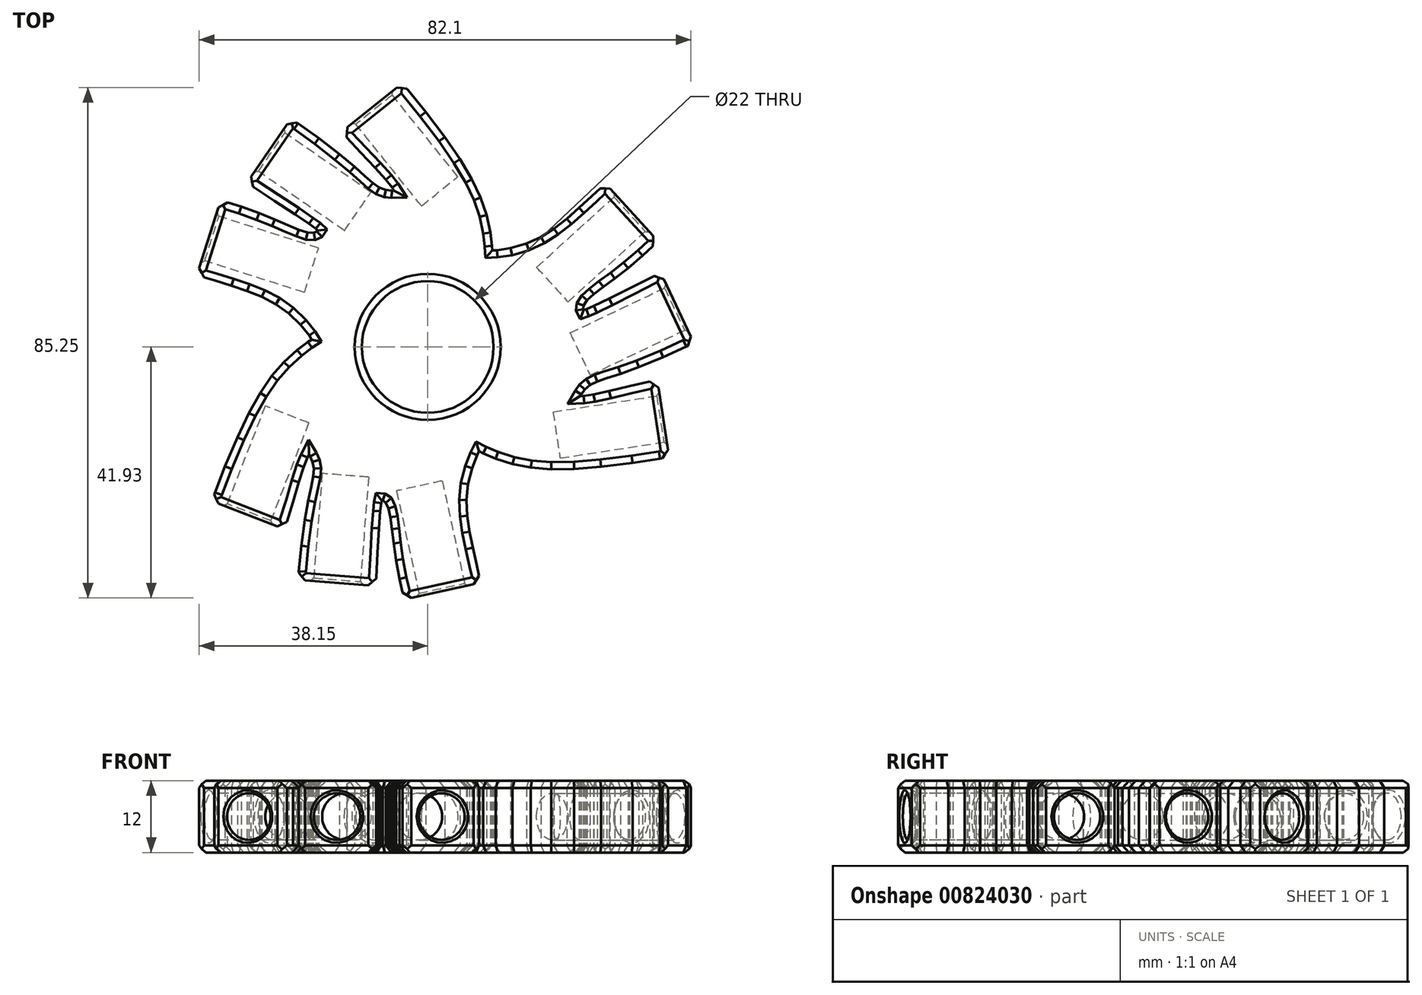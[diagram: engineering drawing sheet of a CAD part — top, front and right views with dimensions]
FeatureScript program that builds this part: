
annotation { "Feature Type Name" : "Feature", "Feature Type Description" : "" }
export const myFeature = defineFeature(function(context is Context, id is Id, definition is map)
    precondition{}
    {
        {
            var Q0;
            Q0=qCreatedBy(makeId("Top.planeOp"),FACE);
            var sketch = newSketch(context, id + "F0", { "sketchPlane" : qUnion([Q0])});
            skLineSegment(sketch, "E0", {"start": v(-3.87, -42.17) * mm, "end": v(8.83, -39.4) * mm});
            skLineSegment(sketch, "E1", {"start": v(8.83, -39.4) * mm, "end": v(8.67, -38.64) * mm});
            skLineSegment(sketch, "E2", {"start": v(8.67, -38.64) * mm, "end": v(8.17, -36.4) * mm});
            skLineSegment(sketch, "E3", {"start": v(8.17, -36.4) * mm, "end": v(7.52, -33.55) * mm});
            skLineSegment(sketch, "E4", {"start": v(7.52, -33.55) * mm, "end": v(6.96, -30.83) * mm});
            skLineSegment(sketch, "E5", {"start": v(6.96, -30.83) * mm, "end": v(6.6, -28.19) * mm});
            skLineSegment(sketch, "E6", {"start": v(6.6, -28.19) * mm, "end": v(6.48, -25.57) * mm});
            skLineSegment(sketch, "E7", {"start": v(6.48, -25.57) * mm, "end": v(6.72, -22.93) * mm});
            skLineSegment(sketch, "E8", {"start": v(6.72, -22.93) * mm, "end": v(7.4, -20.23) * mm});
            skLineSegment(sketch, "E9", {"start": v(7.4, -20.23) * mm, "end": v(8.24, -18.1) * mm});
            skLineSegment(sketch, "E10", {"start": v(8.24, -18.1) * mm, "end": v(8.6, -17.42) * mm});
            skLineSegment(sketch, "E11", {"start": v(8.6, -17.42) * mm, "end": v(9.26, -17.76) * mm});
            skLineSegment(sketch, "E12", {"start": v(9.26, -17.76) * mm, "end": v(11.34, -18.65) * mm});
            skLineSegment(sketch, "E13", {"start": v(11.34, -18.65) * mm, "end": v(14.16, -19.56) * mm});
            skLineSegment(sketch, "E14", {"start": v(14.16, -19.56) * mm, "end": v(17.2, -20.15) * mm});
            skLineSegment(sketch, "E15", {"start": v(17.2, -20.15) * mm, "end": v(20.6, -20.42) * mm});
            skLineSegment(sketch, "E16", {"start": v(20.6, -20.42) * mm, "end": v(24.46, -20.37) * mm});
            skLineSegment(sketch, "E17", {"start": v(24.46, -20.37) * mm, "end": v(28.95, -20.02) * mm});
            skLineSegment(sketch, "E18", {"start": v(28.95, -20.02) * mm, "end": v(34.19, -19.35) * mm});
            skLineSegment(sketch, "E19", {"start": v(34.19, -19.35) * mm, "end": v(38.78, -18.65) * mm});
            skLineSegment(sketch, "E20", {"start": v(38.78, -18.65) * mm, "end": v(40.3, -18.39) * mm});
            skLineSegment(sketch, "E21", {"start": v(40.3, -18.39) * mm, "end": v(38.33, -5.54) * mm});
            skLineSegment(sketch, "E22", {"start": v(38.33, -5.54) * mm, "end": v(37.16, -5.78) * mm});
            skLineSegment(sketch, "E23", {"start": v(37.16, -5.78) * mm, "end": v(33.7, -6.57) * mm});
            skLineSegment(sketch, "E24", {"start": v(33.7, -6.57) * mm, "end": v(30.3, -7.38) * mm});
            skLineSegment(sketch, "E25", {"start": v(30.3, -7.38) * mm, "end": v(27.7, -7.94) * mm});
            skLineSegment(sketch, "E26", {"start": v(27.7, -7.94) * mm, "end": v(26.02, -8.19) * mm});
            skLineSegment(sketch, "E27", {"start": v(26.02, -8.19) * mm, "end": v(25.45, -8.22) * mm});
            skLineSegment(sketch, "E28", {"start": v(25.45, -8.22) * mm, "end": v(25.62, -7.92) * mm});
            skLineSegment(sketch, "E29", {"start": v(25.62, -7.92) * mm, "end": v(26.22, -7.09) * mm});
            skLineSegment(sketch, "E30", {"start": v(26.22, -7.09) * mm, "end": v(27.1, -6.34) * mm});
            skLineSegment(sketch, "E31", {"start": v(27.1, -6.34) * mm, "end": v(28.29, -5.78) * mm});
            skLineSegment(sketch, "E32", {"start": v(28.29, -5.78) * mm, "end": v(29.92, -5.22) * mm});
            skLineSegment(sketch, "E33", {"start": v(29.92, -5.22) * mm, "end": v(32.2, -4.48) * mm});
            skLineSegment(sketch, "E34", {"start": v(32.2, -4.48) * mm, "end": v(35.26, -3.38) * mm});
            skLineSegment(sketch, "E35", {"start": v(35.26, -3.38) * mm, "end": v(39.3, -1.73) * mm});
            skLineSegment(sketch, "E36", {"start": v(39.3, -1.73) * mm, "end": v(43.18, 0.04) * mm});
            skLineSegment(sketch, "E37", {"start": v(43.18, 0.04) * mm, "end": v(44.46, 0.66) * mm});
            skLineSegment(sketch, "E38", {"start": v(44.46, 0.66) * mm, "end": v(38.88, 12.4) * mm});
            skLineSegment(sketch, "E39", {"start": v(38.88, 12.4) * mm, "end": v(37.64, 11.78) * mm});
            skLineSegment(sketch, "E40", {"start": v(37.64, 11.78) * mm, "end": v(33.94, 9.92) * mm});
            skLineSegment(sketch, "E41", {"start": v(33.94, 9.92) * mm, "end": v(30.3, 8.08) * mm});
            skLineSegment(sketch, "E42", {"start": v(30.3, 8.08) * mm, "end": v(27.73, 6.83) * mm});
            skLineSegment(sketch, "E43", {"start": v(27.73, 6.83) * mm, "end": v(26.49, 6.28) * mm});
            skLineSegment(sketch, "E44", {"start": v(26.49, 6.28) * mm, "end": v(26.06, 6.14) * mm});
            skLineSegment(sketch, "E45", {"start": v(26.06, 6.14) * mm, "end": v(25.98, 6.3) * mm});
            skLineSegment(sketch, "E46", {"start": v(25.98, 6.3) * mm, "end": v(26.03, 6.93) * mm});
            skLineSegment(sketch, "E47", {"start": v(26.03, 6.93) * mm, "end": v(26.62, 7.8) * mm});
            skLineSegment(sketch, "E48", {"start": v(26.62, 7.8) * mm, "end": v(27.73, 8.8) * mm});
            skLineSegment(sketch, "E49", {"start": v(27.73, 8.8) * mm, "end": v(29.3, 10) * mm});
            skLineSegment(sketch, "E50", {"start": v(29.3, 10) * mm, "end": v(31.24, 11.44) * mm});
            skLineSegment(sketch, "E51", {"start": v(31.24, 11.44) * mm, "end": v(33.46, 13.17) * mm});
            skLineSegment(sketch, "E52", {"start": v(33.46, 13.17) * mm, "end": v(35.89, 15.24) * mm});
            skLineSegment(sketch, "E53", {"start": v(35.89, 15.24) * mm, "end": v(37.83, 17.06) * mm});
            skLineSegment(sketch, "E54", {"start": v(37.83, 17.06) * mm, "end": v(38.44, 17.7) * mm});
            skLineSegment(sketch, "E55", {"start": v(38.44, 17.7) * mm, "end": v(29.69, 27.3) * mm});
            skLineSegment(sketch, "E56", {"start": v(29.69, 27.3) * mm, "end": v(29.11, 26.8) * mm});
            skLineSegment(sketch, "E57", {"start": v(29.11, 26.8) * mm, "end": v(27.42, 25.23) * mm});
            skLineSegment(sketch, "E58", {"start": v(27.42, 25.23) * mm, "end": v(25.28, 23.25) * mm});
            skLineSegment(sketch, "E59", {"start": v(25.28, 23.25) * mm, "end": v(23.2, 21.41) * mm});
            skLineSegment(sketch, "E60", {"start": v(23.2, 21.41) * mm, "end": v(21.1, 19.77) * mm});
            skLineSegment(sketch, "E61", {"start": v(21.1, 19.77) * mm, "end": v(18.89, 18.37) * mm});
            skLineSegment(sketch, "E62", {"start": v(18.89, 18.37) * mm, "end": v(16.48, 17.26) * mm});
            skLineSegment(sketch, "E63", {"start": v(16.48, 17.26) * mm, "end": v(13.8, 16.5) * mm});
            skLineSegment(sketch, "E64", {"start": v(13.8, 16.5) * mm, "end": v(11.53, 16.15) * mm});
            skLineSegment(sketch, "E65", {"start": v(11.53, 16.15) * mm, "end": v(10.77, 16.12) * mm});
            skLineSegment(sketch, "E66", {"start": v(10.77, 16.12) * mm, "end": v(10.73, 16.87) * mm});
            skLineSegment(sketch, "E67", {"start": v(10.73, 16.87) * mm, "end": v(10.47, 19.11) * mm});
            skLineSegment(sketch, "E68", {"start": v(10.47, 19.11) * mm, "end": v(9.84, 22.01) * mm});
            skLineSegment(sketch, "E69", {"start": v(9.84, 22.01) * mm, "end": v(8.83, 24.94) * mm});
            skLineSegment(sketch, "E70", {"start": v(8.83, 24.94) * mm, "end": v(7.37, 28) * mm});
            skLineSegment(sketch, "E71", {"start": v(7.37, 28) * mm, "end": v(5.4, 31.34) * mm});
            skLineSegment(sketch, "E72", {"start": v(5.4, 31.34) * mm, "end": v(2.84, 35.05) * mm});
            skLineSegment(sketch, "E73", {"start": v(2.84, 35.05) * mm, "end": v(-0.35, 39.25) * mm});
            skLineSegment(sketch, "E74", {"start": v(-0.35, 39.25) * mm, "end": v(-3.26, 42.87) * mm});
            skLineSegment(sketch, "E75", {"start": v(-3.26, 42.87) * mm, "end": v(-4.24, 44.06) * mm});
            skLineSegment(sketch, "E76", {"start": v(-4.24, 44.06) * mm, "end": v(-14.38, 35.92) * mm});
            skLineSegment(sketch, "E77", {"start": v(-14.38, 35.92) * mm, "end": v(-13.6, 35.04) * mm});
            skLineSegment(sketch, "E78", {"start": v(-13.6, 35.04) * mm, "end": v(-11.17, 32.43) * mm});
            skLineSegment(sketch, "E79", {"start": v(-11.17, 32.43) * mm, "end": v(-8.77, 29.9) * mm});
            skLineSegment(sketch, "E80", {"start": v(-8.77, 29.9) * mm, "end": v(-7, 27.93) * mm});
            skLineSegment(sketch, "E81", {"start": v(-7, 27.93) * mm, "end": v(-5.94, 26.59) * mm});
            skLineSegment(sketch, "E82", {"start": v(-5.94, 26.59) * mm, "end": v(-5.63, 26.11) * mm});
            skLineSegment(sketch, "E83", {"start": v(-5.63, 26.11) * mm, "end": v(-5.97, 26.1) * mm});
            skLineSegment(sketch, "E84", {"start": v(-5.97, 26.1) * mm, "end": v(-6.99, 26.21) * mm});
            skLineSegment(sketch, "E85", {"start": v(-6.99, 26.21) * mm, "end": v(-8.08, 26.6) * mm});
            skLineSegment(sketch, "E86", {"start": v(-8.08, 26.6) * mm, "end": v(-9.16, 27.35) * mm});
            skLineSegment(sketch, "E87", {"start": v(-9.16, 27.35) * mm, "end": v(-10.46, 28.5) * mm});
            skLineSegment(sketch, "E88", {"start": v(-10.46, 28.5) * mm, "end": v(-12.23, 30.09) * mm});
            skLineSegment(sketch, "E89", {"start": v(-12.23, 30.09) * mm, "end": v(-14.72, 32.2) * mm});
            skLineSegment(sketch, "E90", {"start": v(-14.72, 32.2) * mm, "end": v(-18.17, 34.86) * mm});
            skLineSegment(sketch, "E91", {"start": v(-18.17, 34.86) * mm, "end": v(-21.64, 37.35) * mm});
            skLineSegment(sketch, "E92", {"start": v(-21.64, 37.35) * mm, "end": v(-22.82, 38.14) * mm});
            skLineSegment(sketch, "E93", {"start": v(-22.82, 38.14) * mm, "end": v(-30.2, 27.43) * mm});
            skLineSegment(sketch, "E94", {"start": v(-30.2, 27.43) * mm, "end": v(-29.04, 26.67) * mm});
            skLineSegment(sketch, "E95", {"start": v(-29.04, 26.67) * mm, "end": v(-25.58, 24.4) * mm});
            skLineSegment(sketch, "E96", {"start": v(-25.58, 24.4) * mm, "end": v(-22.16, 22.16) * mm});
            skLineSegment(sketch, "E97", {"start": v(-22.16, 22.16) * mm, "end": v(-19.8, 20.56) * mm});
            skLineSegment(sketch, "E98", {"start": v(-19.8, 20.56) * mm, "end": v(-18.7, 19.76) * mm});
            skLineSegment(sketch, "E99", {"start": v(-18.7, 19.76) * mm, "end": v(-18.36, 19.46) * mm});
            skLineSegment(sketch, "E100", {"start": v(-18.36, 19.46) * mm, "end": v(-18.46, 19.31) * mm});
            skLineSegment(sketch, "E101", {"start": v(-18.46, 19.31) * mm, "end": v(-19.03, 19.04) * mm});
            skLineSegment(sketch, "E102", {"start": v(-19.03, 19.04) * mm, "end": v(-20.08, 19.11) * mm});
            skLineSegment(sketch, "E103", {"start": v(-20.08, 19.11) * mm, "end": v(-21.51, 19.58) * mm});
            skLineSegment(sketch, "E104", {"start": v(-21.51, 19.58) * mm, "end": v(-23.33, 20.34) * mm});
            skLineSegment(sketch, "E105", {"start": v(-23.33, 20.34) * mm, "end": v(-25.54, 21.3) * mm});
            skLineSegment(sketch, "E106", {"start": v(-25.54, 21.3) * mm, "end": v(-28.15, 22.36) * mm});
            skLineSegment(sketch, "E107", {"start": v(-28.15, 22.36) * mm, "end": v(-31.16, 23.43) * mm});
            skLineSegment(sketch, "E108", {"start": v(-31.16, 23.43) * mm, "end": v(-33.7, 24.2) * mm});
            skLineSegment(sketch, "E109", {"start": v(-33.7, 24.2) * mm, "end": v(-34.56, 24.4) * mm});
            skLineSegment(sketch, "E110", {"start": v(-34.56, 24.4) * mm, "end": v(-38.5, 12.02) * mm});
            skLineSegment(sketch, "E111", {"start": v(-38.5, 12.02) * mm, "end": v(-37.78, 11.78) * mm});
            skLineSegment(sketch, "E112", {"start": v(-37.78, 11.78) * mm, "end": v(-35.58, 11.1) * mm});
            skLineSegment(sketch, "E113", {"start": v(-35.58, 11.1) * mm, "end": v(-32.8, 10.23) * mm});
            skLineSegment(sketch, "E114", {"start": v(-32.8, 10.23) * mm, "end": v(-30.16, 9.35) * mm});
            skLineSegment(sketch, "E115", {"start": v(-30.16, 9.35) * mm, "end": v(-27.69, 8.35) * mm});
            skLineSegment(sketch, "E116", {"start": v(-27.69, 8.35) * mm, "end": v(-25.36, 7.14) * mm});
            skLineSegment(sketch, "E117", {"start": v(-25.36, 7.14) * mm, "end": v(-23.2, 5.61) * mm});
            skLineSegment(sketch, "E118", {"start": v(-23.2, 5.61) * mm, "end": v(-21.2, 3.68) * mm});
            skLineSegment(sketch, "E119", {"start": v(-21.2, 3.68) * mm, "end": v(-19.77, 1.88) * mm});
            skLineSegment(sketch, "E120", {"start": v(-19.77, 1.88) * mm, "end": v(-19.36, 1.24) * mm});
            skLineSegment(sketch, "E121", {"start": v(-19.36, 1.24) * mm, "end": v(-20, 0.83) * mm});
            skLineSegment(sketch, "E122", {"start": v(-20, 0.83) * mm, "end": v(-21.8, -0.52) * mm});
            skLineSegment(sketch, "E123", {"start": v(-21.8, -0.52) * mm, "end": v(-24, -2.52) * mm});
            skLineSegment(sketch, "E124", {"start": v(-24, -2.52) * mm, "end": v(-26.03, -4.86) * mm});
            skLineSegment(sketch, "E125", {"start": v(-26.03, -4.86) * mm, "end": v(-27.96, -7.66) * mm});
            skLineSegment(sketch, "E126", {"start": v(-27.96, -7.66) * mm, "end": v(-29.85, -11.03) * mm});
            skLineSegment(sketch, "E127", {"start": v(-29.85, -11.03) * mm, "end": v(-31.79, -15.1) * mm});
            skLineSegment(sketch, "E128", {"start": v(-31.79, -15.1) * mm, "end": v(-33.83, -19.96) * mm});
            skLineSegment(sketch, "E129", {"start": v(-33.83, -19.96) * mm, "end": v(-35.51, -24.3) * mm});
            skLineSegment(sketch, "E130", {"start": v(-35.51, -24.3) * mm, "end": v(-36.05, -25.74) * mm});
            skLineSegment(sketch, "E131", {"start": v(-36.05, -25.74) * mm, "end": v(-23.94, -30.45) * mm});
            skLineSegment(sketch, "E132", {"start": v(-23.94, -30.45) * mm, "end": v(-23.57, -29.33) * mm});
            skLineSegment(sketch, "E133", {"start": v(-23.57, -29.33) * mm, "end": v(-22.52, -25.92) * mm});
            skLineSegment(sketch, "E134", {"start": v(-22.52, -25.92) * mm, "end": v(-21.52, -22.58) * mm});
            skLineSegment(sketch, "E135", {"start": v(-21.52, -22.58) * mm, "end": v(-20.7, -20.06) * mm});
            skLineSegment(sketch, "E136", {"start": v(-20.7, -20.06) * mm, "end": v(-20.07, -18.47) * mm});
            skLineSegment(sketch, "E137", {"start": v(-20.07, -18.47) * mm, "end": v(-19.82, -17.97) * mm});
            skLineSegment(sketch, "E138", {"start": v(-19.82, -17.97) * mm, "end": v(-19.64, -18.26) * mm});
            skLineSegment(sketch, "E139", {"start": v(-19.64, -18.26) * mm, "end": v(-19.23, -19.2) * mm});
            skLineSegment(sketch, "E140", {"start": v(-19.23, -19.2) * mm, "end": v(-19.02, -20.34) * mm});
            skLineSegment(sketch, "E141", {"start": v(-19.02, -20.34) * mm, "end": v(-19.12, -21.64) * mm});
            skLineSegment(sketch, "E142", {"start": v(-19.12, -21.64) * mm, "end": v(-19.46, -23.34) * mm});
            skLineSegment(sketch, "E143", {"start": v(-19.46, -23.34) * mm, "end": v(-19.96, -25.67) * mm});
            skLineSegment(sketch, "E144", {"start": v(-19.96, -25.67) * mm, "end": v(-20.53, -28.88) * mm});
            skLineSegment(sketch, "E145", {"start": v(-20.53, -28.88) * mm, "end": v(-21.12, -33.2) * mm});
            skLineSegment(sketch, "E146", {"start": v(-21.12, -33.2) * mm, "end": v(-21.54, -37.45) * mm});
            skLineSegment(sketch, "E147", {"start": v(-21.54, -37.45) * mm, "end": v(-21.64, -38.87) * mm});
            skLineSegment(sketch, "E148", {"start": v(-21.64, -38.87) * mm, "end": v(-8.68, -39.9) * mm});
            skLineSegment(sketch, "E149", {"start": v(-8.68, -39.9) * mm, "end": v(-8.6, -38.52) * mm});
            skLineSegment(sketch, "E150", {"start": v(-8.6, -38.52) * mm, "end": v(-8.36, -34.39) * mm});
            skLineSegment(sketch, "E151", {"start": v(-8.36, -34.39) * mm, "end": v(-8.13, -30.3) * mm});
            skLineSegment(sketch, "E152", {"start": v(-8.13, -30.3) * mm, "end": v(-7.92, -27.46) * mm});
            skLineSegment(sketch, "E153", {"start": v(-7.92, -27.46) * mm, "end": v(-7.78, -26.11) * mm});
            skLineSegment(sketch, "E154", {"start": v(-7.78, -26.11) * mm, "end": v(-7.69, -25.67) * mm});
            skLineSegment(sketch, "E155", {"start": v(-7.69, -25.67) * mm, "end": v(-7.51, -25.68) * mm});
            skLineSegment(sketch, "E156", {"start": v(-7.51, -25.68) * mm, "end": v(-7, -26.04) * mm});
            skLineSegment(sketch, "E157", {"start": v(-7, -26.04) * mm, "end": v(-6.53, -26.98) * mm});
            skLineSegment(sketch, "E158", {"start": v(-6.53, -26.98) * mm, "end": v(-6.22, -28.45) * mm});
            skLineSegment(sketch, "E159", {"start": v(-6.22, -28.45) * mm, "end": v(-5.96, -30.41) * mm});
            skLineSegment(sketch, "E160", {"start": v(-5.96, -30.41) * mm, "end": v(-5.69, -32.8) * mm});
            skLineSegment(sketch, "E161", {"start": v(-5.69, -32.8) * mm, "end": v(-5.3, -35.6) * mm});
            skLineSegment(sketch, "E162", {"start": v(-5.3, -35.6) * mm, "end": v(-4.73, -38.73) * mm});
            skLineSegment(sketch, "E163", {"start": v(-4.73, -38.73) * mm, "end": v(-4.12, -41.32) * mm});
            skLineSegment(sketch, "E164", {"start": v(-4.12, -41.32) * mm, "end": v(-3.87, -42.17) * mm});
            skCircle(sketch, "E165", {"center": v(0, 0) * mm, "radius": 11 * mm});
            skSolve(sketch);
        }
        {
            var Q0;
            Q0=makeQuery(id+"F0.imprint","IMPRINT",FACE,{"disambiguationData":[TD([[makeQuery(id+"F0.imprint","IMPRINT",EDGE,{"derivedFrom":sQuery(id+"F0.wireOp",EDGE,"E0")}),1.0]])]});
            extrude(context, id + "F1", {"entities" : qUnion([Q0]), "endBound" : BoundingType.SYMMETRIC, "depth" : 12 * mm, "offsetDistance" : 25 * mm});
        }
        {
            var Q0;
            Q0=makeQuery(id+"F1.opExtrude","CAP_FACE",FACE,{"disambiguationData":[OSD([sQuery(id+"F0.wireOp",EDGE,"E0"),sQuery(id+"F0.wireOp",EDGE,"E1"),sQuery(id+"F0.wireOp",EDGE,"E2"),sQuery(id+"F0.wireOp",EDGE,"E3"),sQuery(id+"F0.wireOp",EDGE,"E4"),sQuery(id+"F0.wireOp",EDGE,"E5"),sQuery(id+"F0.wireOp",EDGE,"E6"),sQuery(id+"F0.wireOp",EDGE,"E7"),sQuery(id+"F0.wireOp",EDGE,"E8"),sQuery(id+"F0.wireOp",EDGE,"E9"),sQuery(id+"F0.wireOp",EDGE,"E10"),sQuery(id+"F0.wireOp",EDGE,"E11"),sQuery(id+"F0.wireOp",EDGE,"E12"),sQuery(id+"F0.wireOp",EDGE,"E13"),sQuery(id+"F0.wireOp",EDGE,"E14"),sQuery(id+"F0.wireOp",EDGE,"E15"),sQuery(id+"F0.wireOp",EDGE,"E16"),sQuery(id+"F0.wireOp",EDGE,"E17"),sQuery(id+"F0.wireOp",EDGE,"E18"),sQuery(id+"F0.wireOp",EDGE,"E19"),sQuery(id+"F0.wireOp",EDGE,"E20"),sQuery(id+"F0.wireOp",EDGE,"E21"),sQuery(id+"F0.wireOp",EDGE,"E22"),sQuery(id+"F0.wireOp",EDGE,"E23"),sQuery(id+"F0.wireOp",EDGE,"E24"),sQuery(id+"F0.wireOp",EDGE,"E25"),sQuery(id+"F0.wireOp",EDGE,"E26"),sQuery(id+"F0.wireOp",EDGE,"E27"),sQuery(id+"F0.wireOp",EDGE,"E28"),sQuery(id+"F0.wireOp",EDGE,"E29"),sQuery(id+"F0.wireOp",EDGE,"E30"),sQuery(id+"F0.wireOp",EDGE,"E31"),sQuery(id+"F0.wireOp",EDGE,"E32"),sQuery(id+"F0.wireOp",EDGE,"E33"),sQuery(id+"F0.wireOp",EDGE,"E34"),sQuery(id+"F0.wireOp",EDGE,"E35"),sQuery(id+"F0.wireOp",EDGE,"E36"),sQuery(id+"F0.wireOp",EDGE,"E37"),sQuery(id+"F0.wireOp",EDGE,"E38"),sQuery(id+"F0.wireOp",EDGE,"E39"),sQuery(id+"F0.wireOp",EDGE,"E40"),sQuery(id+"F0.wireOp",EDGE,"E41"),sQuery(id+"F0.wireOp",EDGE,"E42"),sQuery(id+"F0.wireOp",EDGE,"E43"),sQuery(id+"F0.wireOp",EDGE,"E44"),sQuery(id+"F0.wireOp",EDGE,"E45"),sQuery(id+"F0.wireOp",EDGE,"E46"),sQuery(id+"F0.wireOp",EDGE,"E47"),sQuery(id+"F0.wireOp",EDGE,"E48"),sQuery(id+"F0.wireOp",EDGE,"E49"),sQuery(id+"F0.wireOp",EDGE,"E50"),sQuery(id+"F0.wireOp",EDGE,"E51"),sQuery(id+"F0.wireOp",EDGE,"E52"),sQuery(id+"F0.wireOp",EDGE,"E53"),sQuery(id+"F0.wireOp",EDGE,"E54"),sQuery(id+"F0.wireOp",EDGE,"E55"),sQuery(id+"F0.wireOp",EDGE,"E56"),sQuery(id+"F0.wireOp",EDGE,"E57"),sQuery(id+"F0.wireOp",EDGE,"E58"),sQuery(id+"F0.wireOp",EDGE,"E59"),sQuery(id+"F0.wireOp",EDGE,"E60"),sQuery(id+"F0.wireOp",EDGE,"E61"),sQuery(id+"F0.wireOp",EDGE,"E62"),sQuery(id+"F0.wireOp",EDGE,"E63"),sQuery(id+"F0.wireOp",EDGE,"E64"),sQuery(id+"F0.wireOp",EDGE,"E65"),sQuery(id+"F0.wireOp",EDGE,"E66"),sQuery(id+"F0.wireOp",EDGE,"E67"),sQuery(id+"F0.wireOp",EDGE,"E68"),sQuery(id+"F0.wireOp",EDGE,"E69"),sQuery(id+"F0.wireOp",EDGE,"E70"),sQuery(id+"F0.wireOp",EDGE,"E71"),sQuery(id+"F0.wireOp",EDGE,"E72"),sQuery(id+"F0.wireOp",EDGE,"E73"),sQuery(id+"F0.wireOp",EDGE,"E74"),sQuery(id+"F0.wireOp",EDGE,"E75"),sQuery(id+"F0.wireOp",EDGE,"E76"),sQuery(id+"F0.wireOp",EDGE,"E77"),sQuery(id+"F0.wireOp",EDGE,"E78"),sQuery(id+"F0.wireOp",EDGE,"E79"),sQuery(id+"F0.wireOp",EDGE,"E80"),sQuery(id+"F0.wireOp",EDGE,"E81"),sQuery(id+"F0.wireOp",EDGE,"E82"),sQuery(id+"F0.wireOp",EDGE,"E83"),sQuery(id+"F0.wireOp",EDGE,"E84"),sQuery(id+"F0.wireOp",EDGE,"E85"),sQuery(id+"F0.wireOp",EDGE,"E86"),sQuery(id+"F0.wireOp",EDGE,"E87"),sQuery(id+"F0.wireOp",EDGE,"E88"),sQuery(id+"F0.wireOp",EDGE,"E89"),sQuery(id+"F0.wireOp",EDGE,"E90"),sQuery(id+"F0.wireOp",EDGE,"E91"),sQuery(id+"F0.wireOp",EDGE,"E92"),sQuery(id+"F0.wireOp",EDGE,"E93"),sQuery(id+"F0.wireOp",EDGE,"E94"),sQuery(id+"F0.wireOp",EDGE,"E95"),sQuery(id+"F0.wireOp",EDGE,"E96"),sQuery(id+"F0.wireOp",EDGE,"E97"),sQuery(id+"F0.wireOp",EDGE,"E98"),sQuery(id+"F0.wireOp",EDGE,"E99"),sQuery(id+"F0.wireOp",EDGE,"E100"),sQuery(id+"F0.wireOp",EDGE,"E101"),sQuery(id+"F0.wireOp",EDGE,"E102"),sQuery(id+"F0.wireOp",EDGE,"E103"),sQuery(id+"F0.wireOp",EDGE,"E104"),sQuery(id+"F0.wireOp",EDGE,"E105"),sQuery(id+"F0.wireOp",EDGE,"E106"),sQuery(id+"F0.wireOp",EDGE,"E107"),sQuery(id+"F0.wireOp",EDGE,"E108"),sQuery(id+"F0.wireOp",EDGE,"E109"),sQuery(id+"F0.wireOp",EDGE,"E110"),sQuery(id+"F0.wireOp",EDGE,"E111"),sQuery(id+"F0.wireOp",EDGE,"E112"),sQuery(id+"F0.wireOp",EDGE,"E113"),sQuery(id+"F0.wireOp",EDGE,"E114"),sQuery(id+"F0.wireOp",EDGE,"E115"),sQuery(id+"F0.wireOp",EDGE,"E116"),sQuery(id+"F0.wireOp",EDGE,"E117"),sQuery(id+"F0.wireOp",EDGE,"E118"),sQuery(id+"F0.wireOp",EDGE,"E119"),sQuery(id+"F0.wireOp",EDGE,"E120"),sQuery(id+"F0.wireOp",EDGE,"E121"),sQuery(id+"F0.wireOp",EDGE,"E122"),sQuery(id+"F0.wireOp",EDGE,"E123"),sQuery(id+"F0.wireOp",EDGE,"E124"),sQuery(id+"F0.wireOp",EDGE,"E125"),sQuery(id+"F0.wireOp",EDGE,"E126"),sQuery(id+"F0.wireOp",EDGE,"E127"),sQuery(id+"F0.wireOp",EDGE,"E128"),sQuery(id+"F0.wireOp",EDGE,"E129"),sQuery(id+"F0.wireOp",EDGE,"E130"),sQuery(id+"F0.wireOp",EDGE,"E131"),sQuery(id+"F0.wireOp",EDGE,"E132"),sQuery(id+"F0.wireOp",EDGE,"E133"),sQuery(id+"F0.wireOp",EDGE,"E134"),sQuery(id+"F0.wireOp",EDGE,"E135"),sQuery(id+"F0.wireOp",EDGE,"E136"),sQuery(id+"F0.wireOp",EDGE,"E137"),sQuery(id+"F0.wireOp",EDGE,"E138"),sQuery(id+"F0.wireOp",EDGE,"E139"),sQuery(id+"F0.wireOp",EDGE,"E140"),sQuery(id+"F0.wireOp",EDGE,"E141"),sQuery(id+"F0.wireOp",EDGE,"E142"),sQuery(id+"F0.wireOp",EDGE,"E143"),sQuery(id+"F0.wireOp",EDGE,"E144"),sQuery(id+"F0.wireOp",EDGE,"E145"),sQuery(id+"F0.wireOp",EDGE,"E146"),sQuery(id+"F0.wireOp",EDGE,"E147"),sQuery(id+"F0.wireOp",EDGE,"E148"),sQuery(id+"F0.wireOp",EDGE,"E149"),sQuery(id+"F0.wireOp",EDGE,"E150"),sQuery(id+"F0.wireOp",EDGE,"E151"),sQuery(id+"F0.wireOp",EDGE,"E152"),sQuery(id+"F0.wireOp",EDGE,"E153"),sQuery(id+"F0.wireOp",EDGE,"E154"),sQuery(id+"F0.wireOp",EDGE,"E155"),sQuery(id+"F0.wireOp",EDGE,"E156"),sQuery(id+"F0.wireOp",EDGE,"E157"),sQuery(id+"F0.wireOp",EDGE,"E158"),sQuery(id+"F0.wireOp",EDGE,"E159"),sQuery(id+"F0.wireOp",EDGE,"E160"),sQuery(id+"F0.wireOp",EDGE,"E161"),sQuery(id+"F0.wireOp",EDGE,"E162"),sQuery(id+"F0.wireOp",EDGE,"E163"),sQuery(id+"F0.wireOp",EDGE,"E164"),sQuery(id+"F0.wireOp",EDGE,"E165")])],"isStart":false});
            var Q1;
            Q1=makeQuery(id+"F1.opExtrude","CAP_FACE",FACE,{"disambiguationData":[OSD([sQuery(id+"F0.wireOp",EDGE,"E0"),sQuery(id+"F0.wireOp",EDGE,"E1"),sQuery(id+"F0.wireOp",EDGE,"E2"),sQuery(id+"F0.wireOp",EDGE,"E3"),sQuery(id+"F0.wireOp",EDGE,"E4"),sQuery(id+"F0.wireOp",EDGE,"E5"),sQuery(id+"F0.wireOp",EDGE,"E6"),sQuery(id+"F0.wireOp",EDGE,"E7"),sQuery(id+"F0.wireOp",EDGE,"E8"),sQuery(id+"F0.wireOp",EDGE,"E9"),sQuery(id+"F0.wireOp",EDGE,"E10"),sQuery(id+"F0.wireOp",EDGE,"E11"),sQuery(id+"F0.wireOp",EDGE,"E12"),sQuery(id+"F0.wireOp",EDGE,"E13"),sQuery(id+"F0.wireOp",EDGE,"E14"),sQuery(id+"F0.wireOp",EDGE,"E15"),sQuery(id+"F0.wireOp",EDGE,"E16"),sQuery(id+"F0.wireOp",EDGE,"E17"),sQuery(id+"F0.wireOp",EDGE,"E18"),sQuery(id+"F0.wireOp",EDGE,"E19"),sQuery(id+"F0.wireOp",EDGE,"E20"),sQuery(id+"F0.wireOp",EDGE,"E21"),sQuery(id+"F0.wireOp",EDGE,"E22"),sQuery(id+"F0.wireOp",EDGE,"E23"),sQuery(id+"F0.wireOp",EDGE,"E24"),sQuery(id+"F0.wireOp",EDGE,"E25"),sQuery(id+"F0.wireOp",EDGE,"E26"),sQuery(id+"F0.wireOp",EDGE,"E27"),sQuery(id+"F0.wireOp",EDGE,"E28"),sQuery(id+"F0.wireOp",EDGE,"E29"),sQuery(id+"F0.wireOp",EDGE,"E30"),sQuery(id+"F0.wireOp",EDGE,"E31"),sQuery(id+"F0.wireOp",EDGE,"E32"),sQuery(id+"F0.wireOp",EDGE,"E33"),sQuery(id+"F0.wireOp",EDGE,"E34"),sQuery(id+"F0.wireOp",EDGE,"E35"),sQuery(id+"F0.wireOp",EDGE,"E36"),sQuery(id+"F0.wireOp",EDGE,"E37"),sQuery(id+"F0.wireOp",EDGE,"E38"),sQuery(id+"F0.wireOp",EDGE,"E39"),sQuery(id+"F0.wireOp",EDGE,"E40"),sQuery(id+"F0.wireOp",EDGE,"E41"),sQuery(id+"F0.wireOp",EDGE,"E42"),sQuery(id+"F0.wireOp",EDGE,"E43"),sQuery(id+"F0.wireOp",EDGE,"E44"),sQuery(id+"F0.wireOp",EDGE,"E45"),sQuery(id+"F0.wireOp",EDGE,"E46"),sQuery(id+"F0.wireOp",EDGE,"E47"),sQuery(id+"F0.wireOp",EDGE,"E48"),sQuery(id+"F0.wireOp",EDGE,"E49"),sQuery(id+"F0.wireOp",EDGE,"E50"),sQuery(id+"F0.wireOp",EDGE,"E51"),sQuery(id+"F0.wireOp",EDGE,"E52"),sQuery(id+"F0.wireOp",EDGE,"E53"),sQuery(id+"F0.wireOp",EDGE,"E54"),sQuery(id+"F0.wireOp",EDGE,"E55"),sQuery(id+"F0.wireOp",EDGE,"E56"),sQuery(id+"F0.wireOp",EDGE,"E57"),sQuery(id+"F0.wireOp",EDGE,"E58"),sQuery(id+"F0.wireOp",EDGE,"E59"),sQuery(id+"F0.wireOp",EDGE,"E60"),sQuery(id+"F0.wireOp",EDGE,"E61"),sQuery(id+"F0.wireOp",EDGE,"E62"),sQuery(id+"F0.wireOp",EDGE,"E63"),sQuery(id+"F0.wireOp",EDGE,"E64"),sQuery(id+"F0.wireOp",EDGE,"E65"),sQuery(id+"F0.wireOp",EDGE,"E66"),sQuery(id+"F0.wireOp",EDGE,"E67"),sQuery(id+"F0.wireOp",EDGE,"E68"),sQuery(id+"F0.wireOp",EDGE,"E69"),sQuery(id+"F0.wireOp",EDGE,"E70"),sQuery(id+"F0.wireOp",EDGE,"E71"),sQuery(id+"F0.wireOp",EDGE,"E72"),sQuery(id+"F0.wireOp",EDGE,"E73"),sQuery(id+"F0.wireOp",EDGE,"E74"),sQuery(id+"F0.wireOp",EDGE,"E75"),sQuery(id+"F0.wireOp",EDGE,"E76"),sQuery(id+"F0.wireOp",EDGE,"E77"),sQuery(id+"F0.wireOp",EDGE,"E78"),sQuery(id+"F0.wireOp",EDGE,"E79"),sQuery(id+"F0.wireOp",EDGE,"E80"),sQuery(id+"F0.wireOp",EDGE,"E81"),sQuery(id+"F0.wireOp",EDGE,"E82"),sQuery(id+"F0.wireOp",EDGE,"E83"),sQuery(id+"F0.wireOp",EDGE,"E84"),sQuery(id+"F0.wireOp",EDGE,"E85"),sQuery(id+"F0.wireOp",EDGE,"E86"),sQuery(id+"F0.wireOp",EDGE,"E87"),sQuery(id+"F0.wireOp",EDGE,"E88"),sQuery(id+"F0.wireOp",EDGE,"E89"),sQuery(id+"F0.wireOp",EDGE,"E90"),sQuery(id+"F0.wireOp",EDGE,"E91"),sQuery(id+"F0.wireOp",EDGE,"E92"),sQuery(id+"F0.wireOp",EDGE,"E93"),sQuery(id+"F0.wireOp",EDGE,"E94"),sQuery(id+"F0.wireOp",EDGE,"E95"),sQuery(id+"F0.wireOp",EDGE,"E96"),sQuery(id+"F0.wireOp",EDGE,"E97"),sQuery(id+"F0.wireOp",EDGE,"E98"),sQuery(id+"F0.wireOp",EDGE,"E99"),sQuery(id+"F0.wireOp",EDGE,"E100"),sQuery(id+"F0.wireOp",EDGE,"E101"),sQuery(id+"F0.wireOp",EDGE,"E102"),sQuery(id+"F0.wireOp",EDGE,"E103"),sQuery(id+"F0.wireOp",EDGE,"E104"),sQuery(id+"F0.wireOp",EDGE,"E105"),sQuery(id+"F0.wireOp",EDGE,"E106"),sQuery(id+"F0.wireOp",EDGE,"E107"),sQuery(id+"F0.wireOp",EDGE,"E108"),sQuery(id+"F0.wireOp",EDGE,"E109"),sQuery(id+"F0.wireOp",EDGE,"E110"),sQuery(id+"F0.wireOp",EDGE,"E111"),sQuery(id+"F0.wireOp",EDGE,"E112"),sQuery(id+"F0.wireOp",EDGE,"E113"),sQuery(id+"F0.wireOp",EDGE,"E114"),sQuery(id+"F0.wireOp",EDGE,"E115"),sQuery(id+"F0.wireOp",EDGE,"E116"),sQuery(id+"F0.wireOp",EDGE,"E117"),sQuery(id+"F0.wireOp",EDGE,"E118"),sQuery(id+"F0.wireOp",EDGE,"E119"),sQuery(id+"F0.wireOp",EDGE,"E120"),sQuery(id+"F0.wireOp",EDGE,"E121"),sQuery(id+"F0.wireOp",EDGE,"E122"),sQuery(id+"F0.wireOp",EDGE,"E123"),sQuery(id+"F0.wireOp",EDGE,"E124"),sQuery(id+"F0.wireOp",EDGE,"E125"),sQuery(id+"F0.wireOp",EDGE,"E126"),sQuery(id+"F0.wireOp",EDGE,"E127"),sQuery(id+"F0.wireOp",EDGE,"E128"),sQuery(id+"F0.wireOp",EDGE,"E129"),sQuery(id+"F0.wireOp",EDGE,"E130"),sQuery(id+"F0.wireOp",EDGE,"E131"),sQuery(id+"F0.wireOp",EDGE,"E132"),sQuery(id+"F0.wireOp",EDGE,"E133"),sQuery(id+"F0.wireOp",EDGE,"E134"),sQuery(id+"F0.wireOp",EDGE,"E135"),sQuery(id+"F0.wireOp",EDGE,"E136"),sQuery(id+"F0.wireOp",EDGE,"E137"),sQuery(id+"F0.wireOp",EDGE,"E138"),sQuery(id+"F0.wireOp",EDGE,"E139"),sQuery(id+"F0.wireOp",EDGE,"E140"),sQuery(id+"F0.wireOp",EDGE,"E141"),sQuery(id+"F0.wireOp",EDGE,"E142"),sQuery(id+"F0.wireOp",EDGE,"E143"),sQuery(id+"F0.wireOp",EDGE,"E144"),sQuery(id+"F0.wireOp",EDGE,"E145"),sQuery(id+"F0.wireOp",EDGE,"E146"),sQuery(id+"F0.wireOp",EDGE,"E147"),sQuery(id+"F0.wireOp",EDGE,"E148"),sQuery(id+"F0.wireOp",EDGE,"E149"),sQuery(id+"F0.wireOp",EDGE,"E150"),sQuery(id+"F0.wireOp",EDGE,"E151"),sQuery(id+"F0.wireOp",EDGE,"E152"),sQuery(id+"F0.wireOp",EDGE,"E153"),sQuery(id+"F0.wireOp",EDGE,"E154"),sQuery(id+"F0.wireOp",EDGE,"E155"),sQuery(id+"F0.wireOp",EDGE,"E156"),sQuery(id+"F0.wireOp",EDGE,"E157"),sQuery(id+"F0.wireOp",EDGE,"E158"),sQuery(id+"F0.wireOp",EDGE,"E159"),sQuery(id+"F0.wireOp",EDGE,"E160"),sQuery(id+"F0.wireOp",EDGE,"E161"),sQuery(id+"F0.wireOp",EDGE,"E162"),sQuery(id+"F0.wireOp",EDGE,"E163"),sQuery(id+"F0.wireOp",EDGE,"E164"),sQuery(id+"F0.wireOp",EDGE,"E165")])],"isStart":true});
            chamfer(context, id + "F2", {"entities" : qUnion([Q0, Q1]), "width" : 1.2 * mm, "tangentPropagation" : true});
        }
        {
            var Q0;
            Q0=makeQuery(id+"F1.opExtrude","SWEPT_EDGE",EDGE,{"disambiguationData":[OSD([sQuery(id+"F0.wireOp",EDGE,"E147"),sQuery(id+"F0.wireOp",EDGE,"E148")])]});
            var Q1;
            Q1=makeQuery(id+"F1.opExtrude","SWEPT_EDGE",EDGE,{"disambiguationData":[OSD([sQuery(id+"F0.wireOp",EDGE,"E148"),sQuery(id+"F0.wireOp",EDGE,"E149")])]});
            var Q2;
            Q2=makeQuery(id+"F1.opExtrude","SWEPT_EDGE",EDGE,{"disambiguationData":[OSD([sQuery(id+"F0.wireOp",EDGE,"E0"),sQuery(id+"F0.wireOp",EDGE,"E164")])]});
            var Q3;
            Q3=makeQuery(id+"F1.opExtrude","SWEPT_EDGE",EDGE,{"disambiguationData":[OSD([sQuery(id+"F0.wireOp",EDGE,"E0"),sQuery(id+"F0.wireOp",EDGE,"E1")])]});
            var Q4;
            Q4=makeQuery(id+"F1.opExtrude","SWEPT_EDGE",EDGE,{"disambiguationData":[OSD([sQuery(id+"F0.wireOp",EDGE,"E130"),sQuery(id+"F0.wireOp",EDGE,"E131")])]});
            var Q5;
            Q5=makeQuery(id+"F1.opExtrude","SWEPT_EDGE",EDGE,{"disambiguationData":[OSD([sQuery(id+"F0.wireOp",EDGE,"E131"),sQuery(id+"F0.wireOp",EDGE,"E132")])]});
            var Q6;
            Q6=makeQuery(id+"F1.opExtrude","SWEPT_EDGE",EDGE,{"disambiguationData":[OSD([sQuery(id+"F0.wireOp",EDGE,"E20"),sQuery(id+"F0.wireOp",EDGE,"E21")])]});
            var Q7;
            Q7=makeQuery(id+"F1.opExtrude","SWEPT_EDGE",EDGE,{"disambiguationData":[OSD([sQuery(id+"F0.wireOp",EDGE,"E21"),sQuery(id+"F0.wireOp",EDGE,"E22")])]});
            var Q8;
            Q8=makeQuery(id+"F1.opExtrude","SWEPT_EDGE",EDGE,{"disambiguationData":[OSD([sQuery(id+"F0.wireOp",EDGE,"E37"),sQuery(id+"F0.wireOp",EDGE,"E38")])]});
            var Q9;
            Q9=makeQuery(id+"F1.opExtrude","SWEPT_EDGE",EDGE,{"disambiguationData":[OSD([sQuery(id+"F0.wireOp",EDGE,"E38"),sQuery(id+"F0.wireOp",EDGE,"E39")])]});
            var Q10;
            Q10=makeQuery(id+"F1.opExtrude","SWEPT_EDGE",EDGE,{"disambiguationData":[OSD([sQuery(id+"F0.wireOp",EDGE,"E54"),sQuery(id+"F0.wireOp",EDGE,"E55")])]});
            var Q11;
            Q11=makeQuery(id+"F1.opExtrude","SWEPT_EDGE",EDGE,{"disambiguationData":[OSD([sQuery(id+"F0.wireOp",EDGE,"E55"),sQuery(id+"F0.wireOp",EDGE,"E56")])]});
            var Q12;
            Q12=makeQuery(id+"F1.opExtrude","SWEPT_EDGE",EDGE,{"disambiguationData":[OSD([sQuery(id+"F0.wireOp",EDGE,"E75"),sQuery(id+"F0.wireOp",EDGE,"E76")])]});
            var Q13;
            Q13=makeQuery(id+"F1.opExtrude","SWEPT_EDGE",EDGE,{"disambiguationData":[OSD([sQuery(id+"F0.wireOp",EDGE,"E76"),sQuery(id+"F0.wireOp",EDGE,"E77")])]});
            var Q14;
            Q14=makeQuery(id+"F1.opExtrude","SWEPT_EDGE",EDGE,{"disambiguationData":[OSD([sQuery(id+"F0.wireOp",EDGE,"E92"),sQuery(id+"F0.wireOp",EDGE,"E93")])]});
            var Q15;
            Q15=makeQuery(id+"F1.opExtrude","SWEPT_EDGE",EDGE,{"disambiguationData":[OSD([sQuery(id+"F0.wireOp",EDGE,"E93"),sQuery(id+"F0.wireOp",EDGE,"E94")])]});
            var Q16;
            Q16=makeQuery(id+"F1.opExtrude","SWEPT_EDGE",EDGE,{"disambiguationData":[OSD([sQuery(id+"F0.wireOp",EDGE,"E109"),sQuery(id+"F0.wireOp",EDGE,"E110")])]});
            var Q17;
            Q17=makeQuery(id+"F1.opExtrude","SWEPT_EDGE",EDGE,{"disambiguationData":[OSD([sQuery(id+"F0.wireOp",EDGE,"E110"),sQuery(id+"F0.wireOp",EDGE,"E111")])]});
            chamfer(context, id + "F3", {"entities" : qUnion([Q0, Q1, Q2, Q3, Q4, Q5, Q6, Q7, Q8, Q9, Q10, Q11, Q12, Q13, Q14, Q15, Q16, Q17]), "width" : 1.2 * mm, "tangentPropagation" : true});
        }
        {
            var Q0;
            Q0=makeQuery(id+"F1.opExtrude","SWEPT_FACE",FACE,{"disambiguationData":[OSD([sQuery(id+"F0.wireOp",EDGE,"E76")])]});
            var sketch = newSketch(context, id + "F4", { "sketchPlane" : qUnion([Q0])});
            skLineSegment(sketch, "E166", {"start": v(-23.07, 0) * mm, "end": v(-12.55, 0) * mm, "construction": true});
            skLineSegment(sketch, "E167", {"start": v(-17.81, 4.8) * mm, "end": v(-17.81, -4.8) * mm, "construction": true});
            skCircle(sketch, "E168", {"center": v(-17.81, 0) * mm, "radius": 3.9 * mm});
            skSolve(sketch);
        }
        {
            var Q0;
            Q0=makeQuery(id+"F4.imprint","IMPRINT",FACE,{"disambiguationData":[TD([[makeQuery(id+"F4.imprint","IMPRINT",EDGE,{"derivedFrom":sQuery(id+"F4.wireOp",EDGE,"E168")}),1.0]])]});
            extrude(context, id + "F5", {"entities" : qUnion([Q0]), "oppositeDirection" : true, "depth" : 18 * mm, "offsetDistance" : 25 * mm, "hasSecondDirection" : true, "secondDirectionOppositeDirection" : false, "secondDirectionDepth" : 1 * mm});
        }
        {
            var Q0;
            Q0=qCreatedBy(makeId("Front.planeOp"),FACE);
            var sketch = newSketch(context, id + "F6", { "sketchPlane" : qUnion([Q0])});
            skLineSegment(sketch, "E169", {"start": v(0, -73.39) * mm, "end": v(0, 72.36) * mm, "construction": true});
            skSolve(sketch);
        }
        {
            var Q0;
            Q0=makeQuery(id+"F5.opExtrude","SWEPT_BODY",BODY,{"disambiguationData":[OSD([sQuery(id+"F4.wireOp",EDGE,"E168")])]});
            var Q1;
            Q1=sQuery(id+"F6.wireOp",EDGE,"E169");
            circularPattern(context, id + "F7", {"operationType" : NewBodyOperationType.REMOVE, "entities" : qUnion([Q0]), "axis" : qUnion([Q1]), "angle" : 360 * degree, "instanceCount" : 3, "equalSpace" : true});
        }
        {
            var Q0;
            Q0=makeQuery(id+"F1.opExtrude","SWEPT_FACE",FACE,{"disambiguationData":[OSD([sQuery(id+"F0.wireOp",EDGE,"E148")])]});
            var sketch = newSketch(context, id + "F8", { "sketchPlane" : qUnion([Q0])});
            skLineSegment(sketch, "E170", {"start": v(-17.28, 0) * mm, "end": v(-6.72, 0) * mm, "construction": true});
            skLineSegment(sketch, "E171", {"start": v(-12, 4.8) * mm, "end": v(-12, -4.8) * mm, "construction": true});
            skCircle(sketch, "E172", {"center": v(-12, 0) * mm, "radius": 3.9 * mm});
            skSolve(sketch);
        }
        {
            var Q0;
            Q0=makeQuery(id+"F8.imprint","IMPRINT",FACE,{"disambiguationData":[TD([[makeQuery(id+"F8.imprint","IMPRINT",EDGE,{"derivedFrom":sQuery(id+"F8.wireOp",EDGE,"E172")}),1.0]])]});
            extrude(context, id + "F9", {"entities" : qUnion([Q0]), "oppositeDirection" : true, "depth" : 18 * mm, "offsetDistance" : 25 * mm, "hasSecondDirection" : true, "secondDirectionOppositeDirection" : false, "secondDirectionDepth" : 1 * mm});
        }
        {
            var Q0;
            Q0=makeQuery(id+"F9.opExtrude","SWEPT_BODY",BODY,{"disambiguationData":[OSD([sQuery(id+"F8.wireOp",EDGE,"E172")])]});
            var Q1;
            Q1=sQuery(id+"F6.wireOp",EDGE,"E169");
            circularPattern(context, id + "F10", {"operationType" : NewBodyOperationType.REMOVE, "entities" : qUnion([Q0]), "axis" : qUnion([Q1]), "angle" : 360 * degree, "instanceCount" : 3, "equalSpace" : true});
        }
        {
            var Q0;
            Q0=makeQuery(id+"F1.opExtrude","SWEPT_FACE",FACE,{"disambiguationData":[OSD([sQuery(id+"F0.wireOp",EDGE,"E0")])]});
            var sketch = newSketch(context, id + "F11", { "sketchPlane" : qUnion([Q0])});
            skLineSegment(sketch, "E173", {"start": v(-11.64, 0) * mm, "end": v(-1, 0) * mm, "construction": true});
            skLineSegment(sketch, "E174", {"start": v(-6.31, 4.8) * mm, "end": v(-6.31, -4.8) * mm, "construction": true});
            skCircle(sketch, "E175", {"center": v(-6.31, 0) * mm, "radius": 3.9 * mm});
            skSolve(sketch);
        }
        {
            var Q0;
            Q0=makeQuery(id+"F11.imprint","IMPRINT",FACE,{"disambiguationData":[TD([[makeQuery(id+"F11.imprint","IMPRINT",EDGE,{"derivedFrom":sQuery(id+"F11.wireOp",EDGE,"E175")}),1.0]])]});
            extrude(context, id + "F12", {"entities" : qUnion([Q0]), "oppositeDirection" : true, "depth" : 18 * mm, "offsetDistance" : 25 * mm, "hasSecondDirection" : true, "secondDirectionOppositeDirection" : false, "secondDirectionDepth" : 1 * mm});
        }
        {
            var Q0;
            Q0=makeQuery(id+"F12.opExtrude","SWEPT_BODY",BODY,{"disambiguationData":[OSD([sQuery(id+"F11.wireOp",EDGE,"E175")])]});
            var Q1;
            Q1=sQuery(id+"F6.wireOp",EDGE,"E169");
            circularPattern(context, id + "F13", {"operationType" : NewBodyOperationType.REMOVE, "entities" : qUnion([Q0]), "axis" : qUnion([Q1]), "angle" : 360 * degree, "instanceCount" : 3, "equalSpace" : true});
        }
        {
            var Q0;
            Q0=makeQuery(id+"F7.boolean.opBoolean","INTERSECT",EDGE,{"derivedFrom":[makeQuery(id+"F1.opExtrude","SWEPT_FACE",FACE,{"disambiguationData":[OSD([sQuery(id+"F0.wireOp",EDGE,"E131")])]}),makeQuery(id+"F7.opPattern","COPY",FACE,{"derivedFrom":makeQuery(id+"F5.opExtrude","SWEPT_FACE",FACE,{"disambiguationData":[OSD([sQuery(id+"F4.wireOp",EDGE,"E168")])]}),"instanceName":"1"})]});
            var Q1;
            Q1=makeQuery(id+"F10.boolean.opBoolean","INTERSECT",EDGE,{"derivedFrom":[makeQuery(id+"F1.opExtrude","SWEPT_FACE",FACE,{"disambiguationData":[OSD([sQuery(id+"F0.wireOp",EDGE,"E148")])]}),makeQuery(id+"F9.opExtrude","SWEPT_FACE",FACE,{"disambiguationData":[OSD([sQuery(id+"F8.wireOp",EDGE,"E172")])]})]});
            var Q2;
            Q2=makeQuery(id+"F13.boolean.opBoolean","INTERSECT",EDGE,{"derivedFrom":[makeQuery(id+"F1.opExtrude","SWEPT_FACE",FACE,{"disambiguationData":[OSD([sQuery(id+"F0.wireOp",EDGE,"E0")])]}),makeQuery(id+"F12.opExtrude","SWEPT_FACE",FACE,{"disambiguationData":[OSD([sQuery(id+"F11.wireOp",EDGE,"E175")])]})]});
            var Q3;
            Q3=makeQuery(id+"F7.boolean.opBoolean","INTERSECT",EDGE,{"derivedFrom":[makeQuery(id+"F1.opExtrude","SWEPT_FACE",FACE,{"disambiguationData":[OSD([sQuery(id+"F0.wireOp",EDGE,"E21")])]}),makeQuery(id+"F7.opPattern","COPY",FACE,{"derivedFrom":makeQuery(id+"F5.opExtrude","SWEPT_FACE",FACE,{"disambiguationData":[OSD([sQuery(id+"F4.wireOp",EDGE,"E168")])]}),"instanceName":"2"})]});
            var Q4;
            Q4=makeQuery(id+"F10.boolean.opBoolean","INTERSECT",EDGE,{"derivedFrom":[makeQuery(id+"F1.opExtrude","SWEPT_FACE",FACE,{"disambiguationData":[OSD([sQuery(id+"F0.wireOp",EDGE,"E38")])]}),makeQuery(id+"F10.opPattern","COPY",FACE,{"derivedFrom":makeQuery(id+"F9.opExtrude","SWEPT_FACE",FACE,{"disambiguationData":[OSD([sQuery(id+"F8.wireOp",EDGE,"E172")])]}),"instanceName":"1"})]});
            var Q5;
            Q5=makeQuery(id+"F13.boolean.opBoolean","INTERSECT",EDGE,{"derivedFrom":[makeQuery(id+"F1.opExtrude","SWEPT_FACE",FACE,{"disambiguationData":[OSD([sQuery(id+"F0.wireOp",EDGE,"E55")])]}),makeQuery(id+"F13.opPattern","COPY",FACE,{"derivedFrom":makeQuery(id+"F12.opExtrude","SWEPT_FACE",FACE,{"disambiguationData":[OSD([sQuery(id+"F11.wireOp",EDGE,"E175")])]}),"instanceName":"1"})]});
            var Q6;
            Q6=makeQuery(id+"F7.boolean.opBoolean","INTERSECT",EDGE,{"derivedFrom":[makeQuery(id+"F1.opExtrude","SWEPT_FACE",FACE,{"disambiguationData":[OSD([sQuery(id+"F0.wireOp",EDGE,"E76")])]}),makeQuery(id+"F5.opExtrude","SWEPT_FACE",FACE,{"disambiguationData":[OSD([sQuery(id+"F4.wireOp",EDGE,"E168")])]})]});
            var Q7;
            Q7=makeQuery(id+"F10.boolean.opBoolean","INTERSECT",EDGE,{"derivedFrom":[makeQuery(id+"F1.opExtrude","SWEPT_FACE",FACE,{"disambiguationData":[OSD([sQuery(id+"F0.wireOp",EDGE,"E93")])]}),makeQuery(id+"F10.opPattern","COPY",FACE,{"derivedFrom":makeQuery(id+"F9.opExtrude","SWEPT_FACE",FACE,{"disambiguationData":[OSD([sQuery(id+"F8.wireOp",EDGE,"E172")])]}),"instanceName":"2"})]});
            var Q8;
            Q8=makeQuery(id+"F13.boolean.opBoolean","INTERSECT",EDGE,{"derivedFrom":[makeQuery(id+"F1.opExtrude","SWEPT_FACE",FACE,{"disambiguationData":[OSD([sQuery(id+"F0.wireOp",EDGE,"E110")])]}),makeQuery(id+"F13.opPattern","COPY",FACE,{"derivedFrom":makeQuery(id+"F12.opExtrude","SWEPT_FACE",FACE,{"disambiguationData":[OSD([sQuery(id+"F11.wireOp",EDGE,"E175")])]}),"instanceName":"2"})]});
            chamfer(context, id + "F14", {"entities" : qUnion([Q0, Q1, Q2, Q3, Q4, Q5, Q6, Q7, Q8]), "width" : 0.5 * mm, "tangentPropagation" : true});
        }
    });
